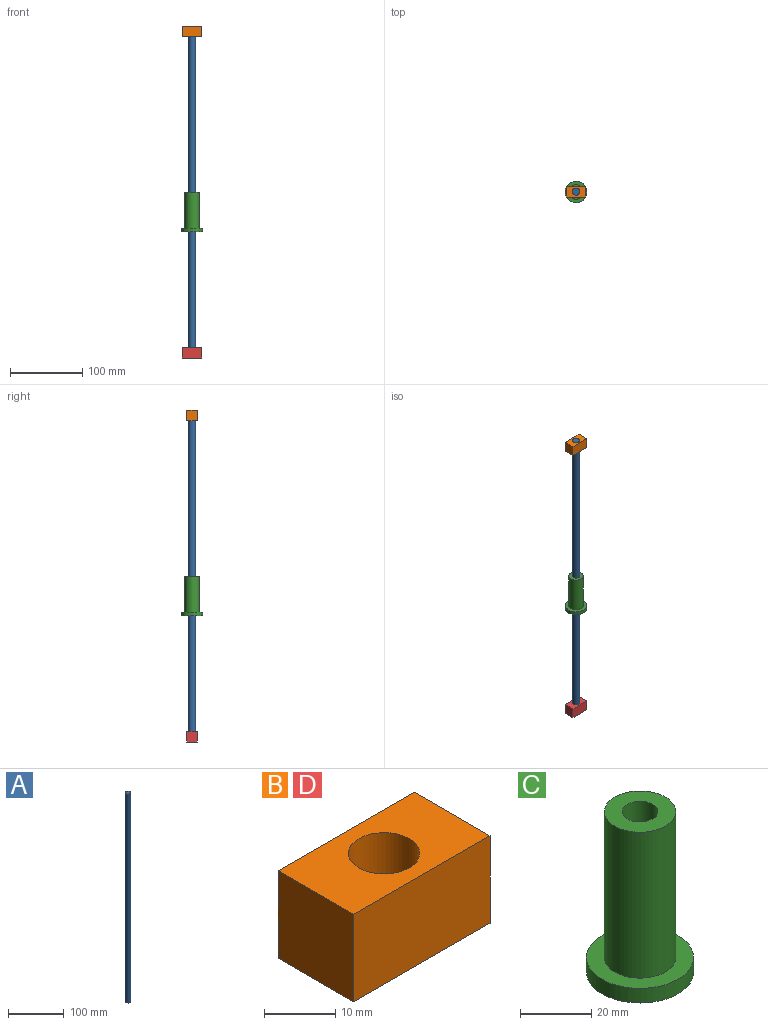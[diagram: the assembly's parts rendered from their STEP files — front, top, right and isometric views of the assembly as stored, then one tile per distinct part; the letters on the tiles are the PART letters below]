
ASSEMBLY  parts=4 mates=3
PART A: 3 faces, bbox 10x10x460 mm
  f0: cylinder r=5mm len=460mm, axis (0,0,-1), area 14451.3mm2, adj f1,f2
  f1: plane 10x10mm, normal (0,0,1), area 78.5mm2, adj f0
  f2: plane 10x10mm, normal (0,0,-1), area 78.5mm2, adj f0
PART B: 7 faces, bbox 27x15x15 mm
  f0: plane 27x15mm, normal (0,-1,0), area 405mm2, adj f1,f4,f5,f6
  f1: plane 15x15mm, normal (1,0,0), area 225mm2, adj f0,f2,f5,f6
  f2: plane 27x15mm, normal (0,1,0), area 405mm2, adj f1,f4,f5,f6
  f3: cylinder r=5mm len=15mm, axis (0,0,-1), area 471.2mm2, adj f5,f6
  f4: plane 15x15mm, normal (-1,0,0), area 225mm2, adj f0,f2,f5,f6
  f5: plane 27x15mm, normal (0,0,1), area 326.5mm2, adj f0,f1,f2,f3,f4
  f6: plane 27x15mm, normal (0,0,-1), area 326.5mm2, adj f0,f1,f2,f3,f4
PART C: 6 faces, bbox 30x30x55 mm
  f0: cylinder r=5mm len=55mm, axis (0,0,-1), area 1727.9mm2, adj f3,f5
  f1: cylinder r=15mm len=30mm, axis (0,0,-1), area 471.2mm2, adj f2,f3
  f2: plane 30x30mm, normal (0,0,1), area 392.7mm2, adj f1,f4
  f3: plane 30x30mm, normal (0,0,-1), area 628.3mm2, adj f0,f1
  f4: cylinder r=10mm len=50mm, axis (0,0,-1), area 3141.6mm2, adj f2,f5
  f5: plane 20x20mm, normal (0,0,1), area 235.6mm2, adj f0,f4
PART D: same geometry as B
PLACE A t=(22.24,21.26,-217.36)mm
PLACE B t=(22.24,21.26,227.64)mm
PLACE C t=(22.24,21.26,-42.36)mm
PLACE D t=(22.24,21.26,-217.36)mm
MATE slider C.f0 <-> A.f0  axis (0,0,1) through (22.24,21.26,12.64)mm
MATE slider B.f3 <-> A.f0  axis (0,0,-1) through (22.24,21.26,242.64)mm
MATE slider D.f3 <-> A.f0  axis (0,0,-1) through (22.24,21.26,-217.36)mm
